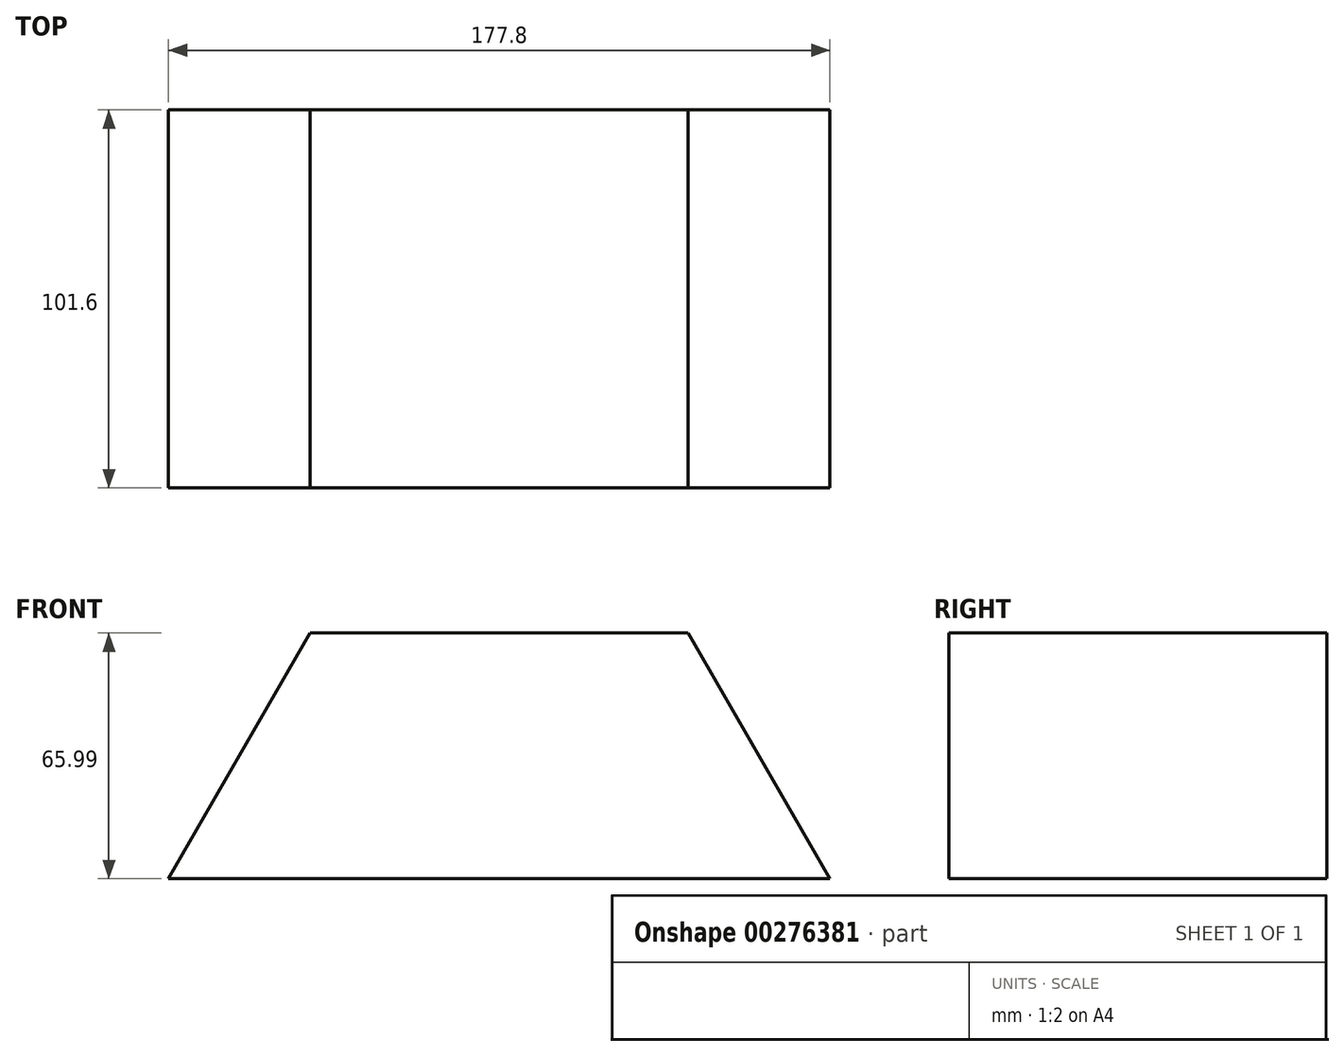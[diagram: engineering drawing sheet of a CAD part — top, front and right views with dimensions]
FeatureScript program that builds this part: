
annotation { "Feature Type Name" : "Feature", "Feature Type Description" : "" }
export const myFeature = defineFeature(function(context is Context, id is Id, definition is map)
    precondition{}
    {
        {
            var Q0;
            Q0=qCreatedBy(makeId("Front.planeOp"),FACE);
            var sketch = newSketch(context, id + "F0", { "sketchPlane" : qUnion([Q0])});
            skLineSegment(sketch, "E0", {"start": v(-24.94, 58.31) * mm, "end": v(76.66, 58.31) * mm});
            skLineSegment(sketch, "E1", {"start": v(76.66, 58.31) * mm, "end": v(114.76, -7.68) * mm});
            skLineSegment(sketch, "E2", {"start": v(114.76, -7.68) * mm, "end": v(-63.04, -7.68) * mm});
            skLineSegment(sketch, "E3", {"start": v(-63.04, -7.68) * mm, "end": v(-24.94, 58.31) * mm});
            skLineSegment(sketch, "E4.bottom", {"start": v(-63.04, -7.68) * mm, "end": v(-37.64, -7.68) * mm});
            skLineSegment(sketch, "E4.top", {"start": v(-63.04, -78.02) * mm, "end": v(-37.64, -78.02) * mm});
            skLineSegment(sketch, "E4.left", {"start": v(-63.04, -7.68) * mm, "end": v(-63.04, -78.02) * mm});
            skLineSegment(sketch, "E4.right", {"start": v(-37.64, -7.68) * mm, "end": v(-37.64, -78.02) * mm});
            skLineSegment(sketch, "E5.bottom", {"start": v(114.76, -7.68) * mm, "end": v(89.36, -7.68) * mm});
            skLineSegment(sketch, "E5.top", {"start": v(114.76, -78.02) * mm, "end": v(89.36, -78.02) * mm});
            skLineSegment(sketch, "E5.left", {"start": v(114.76, -7.68) * mm, "end": v(114.76, -78.02) * mm});
            skLineSegment(sketch, "E5.right", {"start": v(89.36, -7.68) * mm, "end": v(89.36, -78.02) * mm});
            skSolve(sketch);
        }
        {
            var Q0;
            Q0=makeQuery(id+"F0.imprint","IMPRINT",FACE,{"disambiguationData":[TD([[makeQuery(id+"F0.imprint","IMPRINT",EDGE,{"derivedFrom":sQuery(id+"F0.wireOp",EDGE,"E4.bottom")}),-1.0]])]});
            var Q1;
            Q1=makeQuery(id+"F0.imprint","IMPRINT",FACE,{"disambiguationData":[TD([[makeQuery(id+"F0.imprint","IMPRINT",EDGE,{"derivedFrom":sQuery(id+"F0.wireOp",EDGE,"E0")}),-1.0]])]});
            var Q2;
            Q2=makeQuery(id+"F0.imprint","IMPRINT",FACE,{"disambiguationData":[TD([[makeQuery(id+"F0.imprint","IMPRINT",EDGE,{"derivedFrom":sQuery(id+"F0.wireOp",EDGE,"E5.bottom")}),1.0]])]});
            extrude(context, id + "F1", {"entities" : qUnion([Q0, Q1, Q2]), "endBound" : BoundingType.SYMMETRIC, "depth" : 101.6 * mm});
        }
    });
